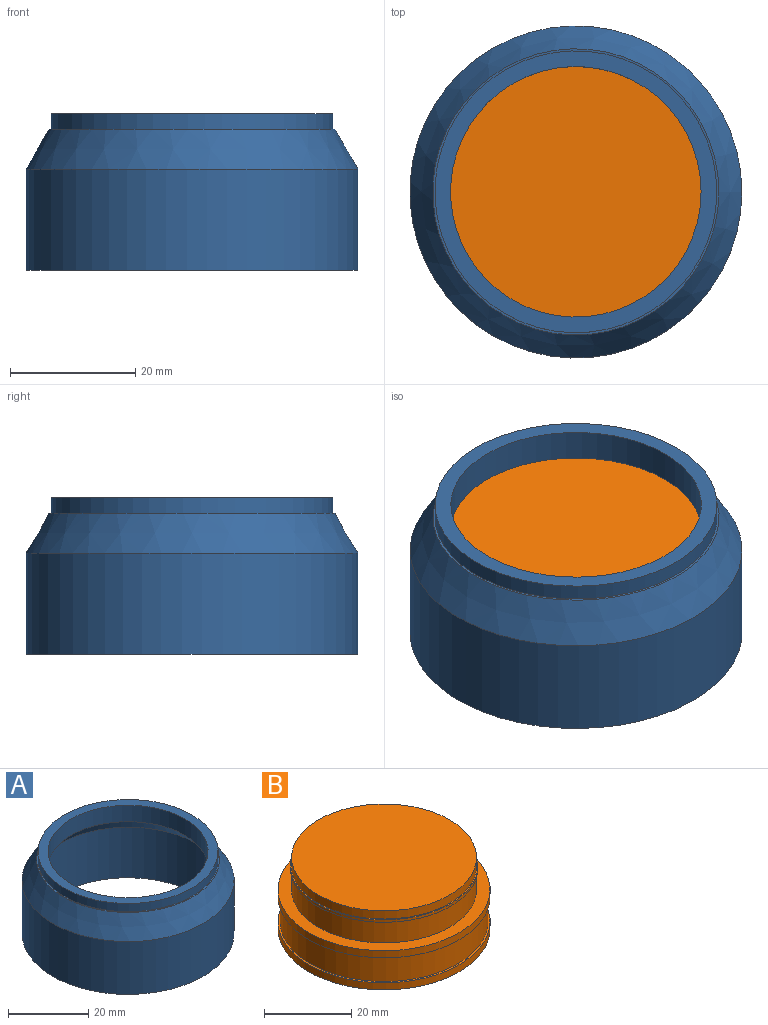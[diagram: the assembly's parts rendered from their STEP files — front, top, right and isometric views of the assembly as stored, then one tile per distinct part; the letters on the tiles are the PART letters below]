
ASSEMBLY  parts=2 mates=1
PART A: 10 faces, bbox 53x53x25 mm
  f0: plane 45.69x45.69mm, normal (0,0,1), area 48.9mm2, adj f1,f9
  f1: cone r=26.5mm half-angle=30deg, axis (0,0,-1), area 1133.7mm2, adj f0,f2
  f2: cylinder r=26.5mm len=53mm, axis (0,0,1), area 2691.8mm2, adj f1,f3
  f3: plane 53x53mm, normal (0,0,-1), area 396.6mm2, adj f2,f4
  f4: cylinder r=24mm len=48mm, axis (0,0,1), area 2336.8mm2, adj f3,f5
  f5: cone r=21.4mm half-angle=30deg, axis (0,0,-1), area 741.7mm2, adj f4,f6
  f6: plane 42.8x42.8mm, normal (0,0,-1), area 182.1mm2, adj f5,f7
  f7: cylinder r=20mm len=40mm, axis (0,0,1), area 628.3mm2, adj f6,f8
  f8: plane 45x45mm, normal (0,0,1), area 333.8mm2, adj f7,f9
  f9: cylinder r=22.5mm len=45mm, axis (0,0,1), area 353.4mm2, adj f0,f8
PART B: 13 faces, bbox 48.6x48.6x20 mm
  f0: plane 48.6x48.6mm, normal (0,0,-1), area 1855.1mm2, adj f12
  f1: plane 42.4x42.4mm, normal (0,0,1), area 1412mm2, adj f2
  f2: cylinder r=21.2mm len=42.4mm, axis (0,0,1), area 306.4mm2, adj f1,f3
  f3: plane 43x43mm, normal (0,0,1), area 40.2mm2, adj f2,f4
  f4: cylinder r=21.5mm len=43mm, axis (0,0,1), area 94.6mm2, adj f3,f5
  f5: plane 43x43mm, normal (0,0,-1), area 40.2mm2, adj f4,f6
  f6: cylinder r=21.2mm len=42.4mm, axis (0,0,1), area 799.2mm2, adj f5,f7
  f7: plane 48.6x48.6mm, normal (0,0,1), area 443.1mm2, adj f6,f8
  f8: cylinder r=24.3mm len=48.6mm, axis (0,0,1), area 305.4mm2, adj f7,f9
  f9: plane 48.6x48.6mm, normal (0,0,-1), area 75.6mm2, adj f8,f10
  f10: cylinder r=23.8mm len=47.6mm, axis (0,0,1), area 1046.8mm2, adj f9,f11
  f11: plane 48.6x48.6mm, normal (0,0,1), area 75.6mm2, adj f10,f12
  f12: cylinder r=24.3mm len=48.6mm, axis (0,0,1), area 305.4mm2, adj f0,f11
PLACE A at identity
PLACE B t=(0,0,-25)mm
MATE fastened B.f2 <-> A.f1  axis (0,0,1) through (0,0,-5)mm
